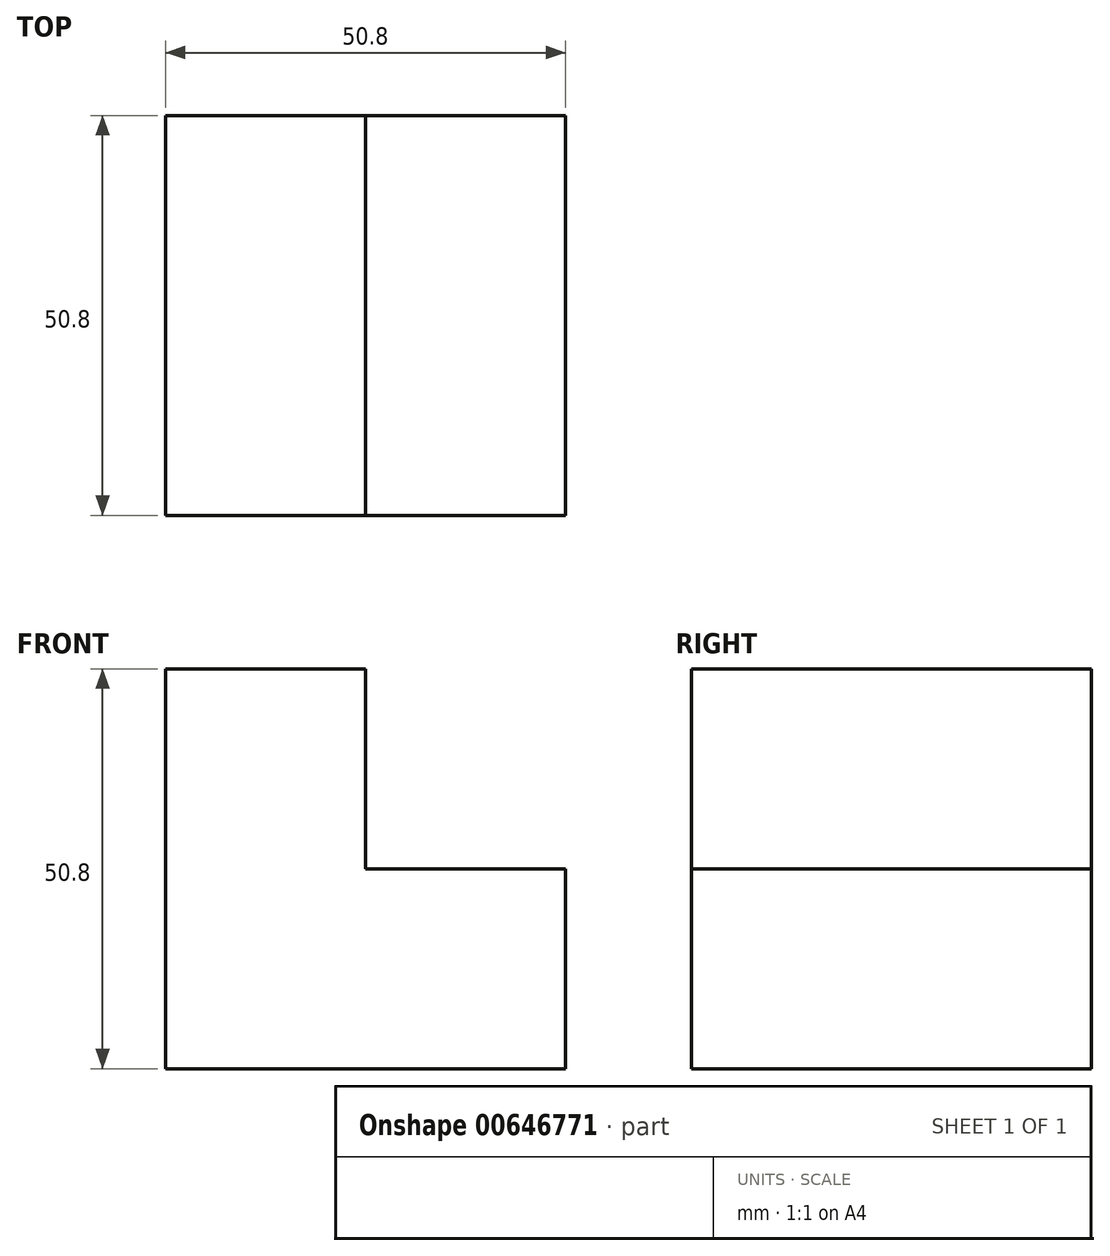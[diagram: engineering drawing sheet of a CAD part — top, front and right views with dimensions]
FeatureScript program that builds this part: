
annotation { "Feature Type Name" : "Feature", "Feature Type Description" : "" }
export const myFeature = defineFeature(function(context is Context, id is Id, definition is map)
    precondition{}
    {
        {
            var Q0;
            Q0=qCreatedBy(makeId("Front.planeOp"),FACE);
            var sketch = newSketch(context, id + "F0", { "sketchPlane" : qUnion([Q0])});
            skLineSegment(sketch, "E0", {"start": v(0, -4.87) * mm, "end": v(-50.8, -4.87) * mm});
            skLineSegment(sketch, "E1", {"start": v(-50.8, -4.87) * mm, "end": v(-50.8, 45.93) * mm});
            skLineSegment(sketch, "E2", {"start": v(-50.8, 45.93) * mm, "end": v(-25.4, 45.93) * mm});
            skLineSegment(sketch, "E3", {"start": v(-25.4, 45.93) * mm, "end": v(-25.4, 20.53) * mm});
            skLineSegment(sketch, "E4", {"start": v(-25.4, 20.53) * mm, "end": v(0, 20.53) * mm});
            skLineSegment(sketch, "E5", {"start": v(0, 20.53) * mm, "end": v(0, -4.87) * mm});
            skSolve(sketch);
        }
        {
            var Q0;
            Q0 = qSketchRegion(id + "F0", true);
            extrude(context, id + "F1", {"entities" : qUnion([Q0]), "depth" : 50.8 * mm, "offsetDistance" : 25.4 * mm});
        }
    });
